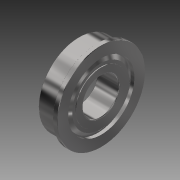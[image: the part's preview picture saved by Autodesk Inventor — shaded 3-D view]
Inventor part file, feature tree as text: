
AUTODESK INVENTOR PART (.ipt)
format: ipt  version: 2014 (Build 180170000, 170)  size: 393,216 bytes
history: native  units: in
note: dims shown in document units (in); Inventor stores cm internally (conversion verified against a paired STEP export)
features: other x4, imported_body x3, extrude x1, fillet x1, sketch x1
ambient origin geometry x8: Origin, YZ Plane, XZ Plane, XY Plane, X Axis, Y Axis, Z Axis, Center Point
bodies: Body1 (feature_tree), Body2 (feature_tree), Body3 (feature_tree)
feature tree (10):
  other  "FR8ZZ"
  other  "FR8ZZ1"
  extrude  "Extrusion1"  Depth=0.01in
  fillet  "Fillet1"  [1 undecoded]
  other  "FR8ZZ_1"
  other  "FR8ZZ_2"
  imported_body  "Base1"
  imported_body  "Base2"
  imported_body  "Base3"
  sketch  "Sketch1"  dims[d0=1.0in d1=0.0in d2=0.01in]
note: 1 required parameter value undecoded (feature->parameter linkage not recoverable at this tier; creation-order binding heuristic only, values carry confidence <= 0.55)
